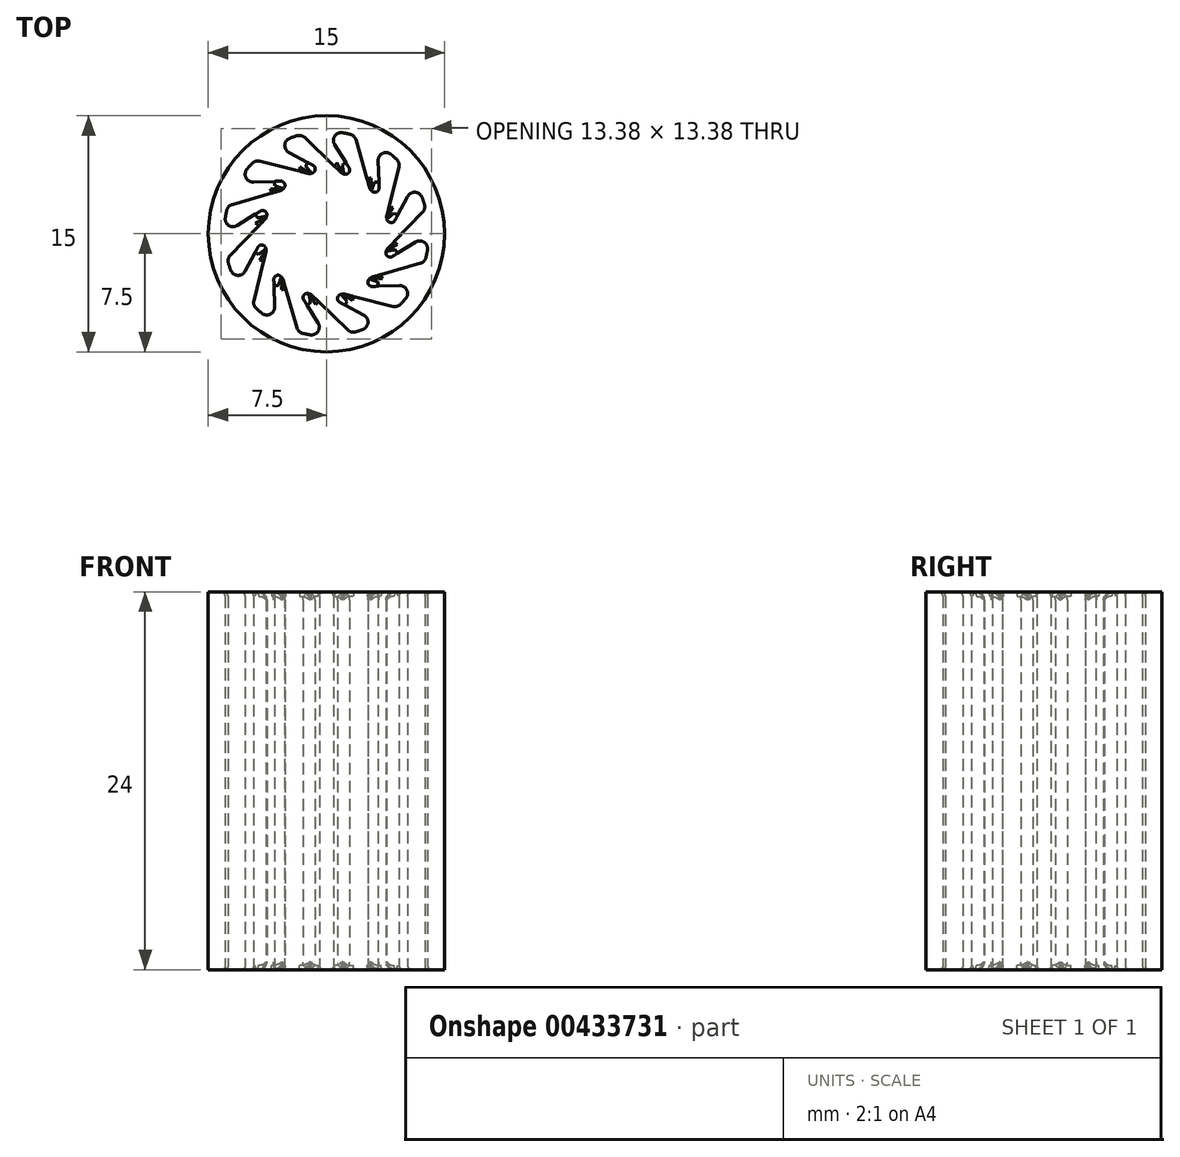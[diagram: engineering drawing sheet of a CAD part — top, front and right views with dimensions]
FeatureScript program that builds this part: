
annotation { "Feature Type Name" : "Feature", "Feature Type Description" : "" }
export const myFeature = defineFeature(function(context is Context, id is Id, definition is map)
    precondition{}
    {
        {
            assignVariable(context, id + "F0", {"name" : "Bearing_length", "anyValue" : 24});
        }
        {
            var Q0;
            Q0=qCreatedBy(makeId("Top.planeOp"),FACE);
            var sketch = newSketch(context, id + "F1", { "sketchPlane" : qUnion([Q0])});
            skCircle(sketch, "E0", {"center": v(0, 0) * mm, "radius": 3.98 * mm, "construction": true});
            skCircle(sketch, "E1", {"center": v(0, 0) * mm, "radius": 7.5 * mm});
            skCircle(sketch, "E2", {"center": v(0, 0) * mm, "radius": 6.5 * mm});
            skLineSegment(sketch, "E3", {"start": v(-1.57, 6.3) * mm, "end": v(0.96, 3.86) * mm});
            skLineSegment(sketch, "E4", {"start": v(0.96, 3.86) * mm, "end": v(1.87, 3.5) * mm});
            skLineSegment(sketch, "E5", {"start": v(1.87, 3.5) * mm, "end": v(0, 6.5) * mm});
            skLineSegment(sketch, "E6", {"start": v(0, 9.18) * mm, "end": v(0, -10.97) * mm, "construction": true});
            skLineSegment(sketch, "E7", {"start": v(-14.87, 0) * mm, "end": v(13.5, 0) * mm, "construction": true});
            skLineSegment(sketch, "E8", {"start": v(0, 0) * mm, "end": v(-1.57, 6.3) * mm, "construction": true});
            skLineSegment(sketch, "E9", {"start": v(1.08, 4.35) * mm, "end": v(0, 0) * mm, "construction": true});
            skLineSegment(sketch, "E10", {"start": v(2.23, 4.19) * mm, "end": v(0, 0) * mm, "construction": true});
            skSolve(sketch);
        }
        {
            var Q0;
            Q0=qCreatedBy(makeId("Right.planeOp"),FACE);
            var sketch = newSketch(context, id + "F2", { "sketchPlane" : qUnion([Q0])});
            skLineSegment(sketch, "E11", {"start": v(0, 50.6) * mm, "end": v(0, -59.8) * mm, "construction": true});
            skSolve(sketch);
        }
        {
            var Q0;
            Q0=makeQuery(id+"F1.imprint","IMPRINT",FACE,{"disambiguationData":[TD([[makeQuery(id+"F1.imprint","IMPRINT",EDGE,{"derivedFrom":sQuery(id+"F1.wireOp",EDGE,"E1")}),1.0]])]});
            var Q1;
            {var subQ0=sQuery(id+"F1.wireOp",EDGE,"E3");Q1=makeQuery(id+"F1.imprint","IMPRINT",FACE,{"disambiguationData":[TD([[makeQuery(id+"F1.imprint","IMPRINT",EDGE,{"derivedFrom":subQ0}),1.0]])]});}
            extrude(context, id + "F3", {"entities" : qUnion([Q0, Q1]), "depth" : (getVariable(context, 'Bearing_length')) * mm});
        }
        {
            var Q0;
            Q0=makeQuery(id+"F3.opExtrude","SWEPT_EDGE",EDGE,{"disambiguationData":[OSD([sQuery(id+"F1.wireOp",EDGE,"E2"),sQuery(id+"F1.wireOp",EDGE,"E3")])]});
            var Q1;
            Q1=makeQuery(id+"F3.opExtrude","SWEPT_EDGE",EDGE,{"disambiguationData":[OSD([sQuery(id+"F1.wireOp",EDGE,"E2"),sQuery(id+"F1.wireOp",EDGE,"E5")])]});
            var Q2;
            Q2=makeQuery(id+"F3.opExtrude","SWEPT_EDGE",EDGE,{"disambiguationData":[OSD([sQuery(id+"F1.wireOp",EDGE,"E3"),sQuery(id+"F1.wireOp",EDGE,"E4")])]});
            var Q3;
            Q3=makeQuery(id+"F3.opExtrude","CAP_EDGE",EDGE,{"disambiguationData":[OSD([sQuery(id+"F1.wireOp",EDGE,"E4")])],"isStart":false});
            var Q4;
            Q4=makeQuery(id+"F3.opExtrude","CAP_EDGE",EDGE,{"disambiguationData":[OSD([sQuery(id+"F1.wireOp",EDGE,"E4")])],"isStart":true});
            fillet(context, id + "F4", {"entities" : qUnion([Q0, Q1, Q2, Q3, Q4]), "radius" : .5 * mm, "tangentPropagation" : true, "allowEdgeOverflow" : false});
        }
        {
            var Q0;
            Q0=makeQuery(id+"F3.opExtrude","SWEPT_EDGE",EDGE,{"disambiguationData":[OSD([sQuery(id+"F1.wireOp",EDGE,"E4"),sQuery(id+"F1.wireOp",EDGE,"E5")])]});
            fillet(context, id + "F5", {"entities" : qUnion([Q0]), "radius" : 0.27 * mm, "tangentPropagation" : true, "allowEdgeOverflow" : false});
        }
        {
            var Q0;
            Q0=makeQuery(id+"F3.opExtrude","SWEPT_FACE",FACE,{"disambiguationData":[OSD([sQuery(id+"F1.wireOp",EDGE,"E5")])]});
            var Q1;
            Q1=makeQuery(id+"F4.opFillet","BLEND_FACE",FACE,{"disambiguationData":[OSD([sQuery(id+"F1.wireOp",EDGE,"E2"),sQuery(id+"F1.wireOp",EDGE,"E5")])]});
            var Q2;
            Q2=makeQuery(id+"F3.opExtrude","SWEPT_FACE",FACE,{"disambiguationData":[OSD([sQuery(id+"F1.wireOp",EDGE,"E3")])]});
            var Q3;
            Q3=makeQuery(id+"F4.opFillet","BLEND_FACE",FACE,{"disambiguationData":[OSD([sQuery(id+"F1.wireOp",EDGE,"E2"),sQuery(id+"F1.wireOp",EDGE,"E3")])]});
            var Q4;
            Q4=makeQuery(id+"F4.opFillet","BLEND_FACE",FACE,{"disambiguationData":[OSD([sQuery(id+"F1.wireOp",EDGE,"E3"),sQuery(id+"F1.wireOp",EDGE,"E4")])]});
            var Q5;
            Q5=makeQuery(id+"F3.opExtrude","SWEPT_FACE",FACE,{"disambiguationData":[OSD([sQuery(id+"F1.wireOp",EDGE,"E4")])]});
            var Q6;
            {var subQ0=sQuery(id+"F1.wireOp",EDGE,"E4");Q6=makeQuery(id+"F4.opFillet","BLEND_FACE",FACE,{"disambiguationData":[OSD([subQ0]),TDD([makeQuery(id+"F3.opExtrude","CAP_EDGE",EDGE,{"disambiguationData":[OSD([subQ0])],"isStart":false})])]});}
            var Q7;
            {var subQ0=sQuery(id+"F1.wireOp",EDGE,"E4");Q7=makeQuery(id+"F4.opFillet","BLEND_FACE",FACE,{"disambiguationData":[OSD([subQ0]),TDD([makeQuery(id+"F3.opExtrude","CAP_EDGE",EDGE,{"disambiguationData":[OSD([subQ0])],"isStart":true})])]});}
            var Q8;
            {var subQ0=sQuery(id+"F1.wireOp",EDGE,"E5");var subQ1=sQuery(id+"F1.wireOp",EDGE,"E4");Q8=makeQuery(id+"F5.opFillet","BLEND_FACE",FACE,{"disambiguationData":[OSD([subQ1,subQ0]),TDD([makeQuery(id+"F3.opExtrude","SWEPT_EDGE",EDGE,{"disambiguationData":[OSD([subQ1,subQ0])]})])]});}
            var Q9;
            {var subQ0=sQuery(id+"F1.wireOp",EDGE,"E5");var subQ1=sQuery(id+"F1.wireOp",EDGE,"E4");Q9=makeQuery(id+"F5.opFillet","BLEND_FACE",FACE,{"disambiguationData":[OSD([subQ1,subQ0]),TDD([makeQuery(id+"F4.opFillet","BLEND_EDGE",EDGE,{"blendedFrom":[makeQuery(id+"F3.opExtrude","CAP_EDGE",EDGE,{"disambiguationData":[OSD([subQ1])],"isStart":false}),makeQuery(id+"F3.opExtrude","SWEPT_FACE",FACE,{"disambiguationData":[OSD([subQ0])]})],"blendedInto":[makeQuery(id+"F3.opExtrude","SWEPT_FACE",FACE,{"disambiguationData":[OSD([subQ0])]})]})])]});}
            var Q10;
            {var subQ0=sQuery(id+"F1.wireOp",EDGE,"E3");var subQ1=sQuery(id+"F1.wireOp",EDGE,"E4");Q10=makeQuery(id+"F5.opFillet","BLEND_FACE",FACE,{"disambiguationData":[OSD([subQ0,subQ1]),TDD([makeQuery(id+"F4.opFillet","BLEND_EDGE",EDGE,{"blendedFrom":[makeQuery(id+"F3.opExtrude","CAP_EDGE",EDGE,{"disambiguationData":[OSD([subQ1])],"isStart":false}),makeQuery(id+"F3.opExtrude","SWEPT_FACE",FACE,{"disambiguationData":[OSD([subQ0])]})],"blendedInto":[makeQuery(id+"F3.opExtrude","SWEPT_FACE",FACE,{"disambiguationData":[OSD([subQ0])]})]})])]});}
            var Q11;
            {var subQ0=sQuery(id+"F1.wireOp",EDGE,"E3");Q11=makeQuery(id+"F5.opFillet","BLEND_FACE",FACE,{"disambiguationData":[OSD([subQ0]),TDD([makeQuery(id+"F3.opExtrude","CAP_EDGE",EDGE,{"disambiguationData":[OSD([subQ0])],"isStart":false})])]});}
            var Q12;
            {var subQ0=sQuery(id+"F1.wireOp",EDGE,"E5");Q12=makeQuery(id+"F5.opFillet","BLEND_FACE",FACE,{"disambiguationData":[OSD([subQ0]),TDD([makeQuery(id+"F3.opExtrude","CAP_EDGE",EDGE,{"disambiguationData":[OSD([subQ0])],"isStart":false})])]});}
            var Q13;
            {var subQ0=sQuery(id+"F1.wireOp",EDGE,"E5");Q13=makeQuery(id+"F5.opFillet","BLEND_FACE",FACE,{"disambiguationData":[OSD([subQ0]),TDD([makeQuery(id+"F3.opExtrude","CAP_EDGE",EDGE,{"disambiguationData":[OSD([subQ0])],"isStart":true})])]});}
            var Q14;
            {var subQ0=sQuery(id+"F1.wireOp",EDGE,"E3");Q14=makeQuery(id+"F5.opFillet","BLEND_FACE",FACE,{"disambiguationData":[OSD([subQ0]),TDD([makeQuery(id+"F3.opExtrude","CAP_EDGE",EDGE,{"disambiguationData":[OSD([subQ0])],"isStart":true})])]});}
            var Q15;
            {var subQ0=sQuery(id+"F1.wireOp",EDGE,"E5");var subQ1=sQuery(id+"F1.wireOp",EDGE,"E4");var subQ2=sQuery(id+"F1.wireOp",EDGE,"E3");var subQ3=sQuery(id+"F1.wireOp",EDGE,"E2");var subQ4=sQuery(id+"F1.wireOp",EDGE,"E1");Q15=makeQuery(id+"F5.opFillet","BLEND_FACE",FACE,{"disambiguationData":[OSD([subQ4,subQ3,subQ2,subQ1,subQ0]),TDD([makeQuery(id+"F4.opFillet","BLEND_EDGE",EDGE,{"blendedFrom":[makeQuery(id+"F3.opExtrude","SWEPT_EDGE",EDGE,{"disambiguationData":[OSD([subQ3,subQ0])]}),makeQuery(id+"F3.opExtrude","CAP_FACE",FACE,{"disambiguationData":[OSD([subQ4,subQ3,subQ2,subQ1,subQ0])],"isStart":false})],"blendedInto":[makeQuery(id+"F3.opExtrude","CAP_FACE",FACE,{"disambiguationData":[OSD([subQ4,subQ3,subQ2,subQ1,subQ0])],"isStart":false})]})])]});}
            var Q16;
            {var subQ0=sQuery(id+"F1.wireOp",EDGE,"E5");var subQ1=sQuery(id+"F1.wireOp",EDGE,"E4");var subQ2=sQuery(id+"F1.wireOp",EDGE,"E3");var subQ3=sQuery(id+"F1.wireOp",EDGE,"E2");var subQ4=sQuery(id+"F1.wireOp",EDGE,"E1");Q16=makeQuery(id+"F5.opFillet","BLEND_FACE",FACE,{"disambiguationData":[OSD([subQ4,subQ3,subQ2,subQ1,subQ0]),TDD([makeQuery(id+"F4.opFillet","BLEND_EDGE",EDGE,{"blendedFrom":[makeQuery(id+"F3.opExtrude","SWEPT_EDGE",EDGE,{"disambiguationData":[OSD([subQ3,subQ0])]}),makeQuery(id+"F3.opExtrude","CAP_FACE",FACE,{"disambiguationData":[OSD([subQ4,subQ3,subQ2,subQ1,subQ0])],"isStart":true})],"blendedInto":[makeQuery(id+"F3.opExtrude","CAP_FACE",FACE,{"disambiguationData":[OSD([subQ4,subQ3,subQ2,subQ1,subQ0])],"isStart":true})]})])]});}
            var Q17;
            {var subQ0=sQuery(id+"F1.wireOp",EDGE,"E5");var subQ1=sQuery(id+"F1.wireOp",EDGE,"E4");var subQ2=sQuery(id+"F1.wireOp",EDGE,"E3");var subQ3=sQuery(id+"F1.wireOp",EDGE,"E2");var subQ4=sQuery(id+"F1.wireOp",EDGE,"E1");Q17=makeQuery(id+"F5.opFillet","BLEND_FACE",FACE,{"disambiguationData":[OSD([subQ4,subQ3,subQ2,subQ1,subQ0]),TDD([makeQuery(id+"F4.opFillet","BLEND_EDGE",EDGE,{"blendedFrom":[makeQuery(id+"F3.opExtrude","SWEPT_EDGE",EDGE,{"disambiguationData":[OSD([subQ3,subQ2])]}),makeQuery(id+"F3.opExtrude","CAP_FACE",FACE,{"disambiguationData":[OSD([subQ4,subQ3,subQ2,subQ1,subQ0])],"isStart":true})],"blendedInto":[makeQuery(id+"F3.opExtrude","CAP_FACE",FACE,{"disambiguationData":[OSD([subQ4,subQ3,subQ2,subQ1,subQ0])],"isStart":true})]})])]});}
            var Q18;
            {var subQ0=sQuery(id+"F1.wireOp",EDGE,"E5");var subQ1=sQuery(id+"F1.wireOp",EDGE,"E4");Q18=makeQuery(id+"F5.opFillet","BLEND_FACE",FACE,{"disambiguationData":[OSD([subQ1,subQ0]),TDD([makeQuery(id+"F4.opFillet","BLEND_EDGE",EDGE,{"blendedFrom":[makeQuery(id+"F3.opExtrude","CAP_EDGE",EDGE,{"disambiguationData":[OSD([subQ1])],"isStart":true}),makeQuery(id+"F3.opExtrude","SWEPT_FACE",FACE,{"disambiguationData":[OSD([subQ0])]})],"blendedInto":[makeQuery(id+"F3.opExtrude","SWEPT_FACE",FACE,{"disambiguationData":[OSD([subQ0])]})]})])]});}
            var Q19;
            {var subQ0=sQuery(id+"F1.wireOp",EDGE,"E5");var subQ1=sQuery(id+"F1.wireOp",EDGE,"E4");var subQ2=sQuery(id+"F1.wireOp",EDGE,"E3");var subQ3=sQuery(id+"F1.wireOp",EDGE,"E2");var subQ4=sQuery(id+"F1.wireOp",EDGE,"E1");Q19=makeQuery(id+"F5.opFillet","BLEND_FACE",FACE,{"disambiguationData":[OSD([subQ4,subQ3,subQ2,subQ1,subQ0]),TDD([makeQuery(id+"F4.opFillet","BLEND_EDGE",EDGE,{"blendedFrom":[makeQuery(id+"F3.opExtrude","SWEPT_EDGE",EDGE,{"disambiguationData":[OSD([subQ3,subQ2])]}),makeQuery(id+"F3.opExtrude","CAP_FACE",FACE,{"disambiguationData":[OSD([subQ4,subQ3,subQ2,subQ1,subQ0])],"isStart":false})],"blendedInto":[makeQuery(id+"F3.opExtrude","CAP_FACE",FACE,{"disambiguationData":[OSD([subQ4,subQ3,subQ2,subQ1,subQ0])],"isStart":false})]})])]});}
            var Q20;
            {var subQ0=sQuery(id+"F1.wireOp",EDGE,"E4");var subQ1=sQuery(id+"F1.wireOp",EDGE,"E3");Q20=makeQuery(id+"F5.opFillet","BLEND_FACE",FACE,{"disambiguationData":[OSD([subQ1,subQ0]),TDD([makeQuery(id+"F4.opFillet","BLEND_EDGE",EDGE,{"blendedFrom":[makeQuery(id+"F3.opExtrude","SWEPT_EDGE",EDGE,{"disambiguationData":[OSD([subQ1,subQ0])]}),makeQuery(id+"F3.opExtrude","CAP_EDGE",EDGE,{"disambiguationData":[OSD([subQ0])],"isStart":false})],"blendedInto":[]})])]});}
            var Q21;
            {var subQ0=sQuery(id+"F1.wireOp",EDGE,"E3");var subQ1=sQuery(id+"F1.wireOp",EDGE,"E4");Q21=makeQuery(id+"F5.opFillet","BLEND_FACE",FACE,{"disambiguationData":[OSD([subQ0,subQ1]),TDD([makeQuery(id+"F4.opFillet","BLEND_EDGE",EDGE,{"blendedFrom":[makeQuery(id+"F3.opExtrude","CAP_EDGE",EDGE,{"disambiguationData":[OSD([subQ1])],"isStart":true}),makeQuery(id+"F3.opExtrude","SWEPT_FACE",FACE,{"disambiguationData":[OSD([subQ0])]})],"blendedInto":[makeQuery(id+"F3.opExtrude","SWEPT_FACE",FACE,{"disambiguationData":[OSD([subQ0])]})]})])]});}
            var Q22;
            {var subQ0=sQuery(id+"F1.wireOp",EDGE,"E4");var subQ1=sQuery(id+"F1.wireOp",EDGE,"E3");Q22=makeQuery(id+"F5.opFillet","BLEND_FACE",FACE,{"disambiguationData":[OSD([subQ1,subQ0]),TDD([makeQuery(id+"F4.opFillet","BLEND_EDGE",EDGE,{"blendedFrom":[makeQuery(id+"F3.opExtrude","SWEPT_EDGE",EDGE,{"disambiguationData":[OSD([subQ1,subQ0])]}),makeQuery(id+"F3.opExtrude","CAP_EDGE",EDGE,{"disambiguationData":[OSD([subQ0])],"isStart":true})],"blendedInto":[]})])]});}
            var Q23;
            Q23=sQuery(id+"F2.wireOp",EDGE,"E11");
            circularPattern(context, id + "F6", {"patternType" : PatternType.FACE, "faces" : qUnion([Q0, Q1, Q2, Q3, Q4, Q5, Q6, Q7, Q8, Q9, Q10, Q11, Q12, Q13, Q14, Q15, Q16, Q17, Q18, Q19, Q20, Q21, Q22]), "axis" : qUnion([Q23]), "angle" : 360 * degree, "instanceCount" : 12, "equalSpace" : true});
        }
    });
